SOLIDWORKS PART (.sldprt)
format: sldprt  version: not decoded by parser v0  size: 187,392 bytes
history: native  units: mm
features: sketch x6, plane x3, hole x2, material x1, extrude x1, cut_extrude x1 (+9 scaffold rows collapsed)
feature tree (23):
  scaffold x9  (default folders/planes/origin — collapsed)
  material  "Matériau <non spécifié>"
  plane  "Plan de face"
  plane  "Plan de dessus"
  plane  "Plan de droite"
  sketch  "Esquisse1"  dims[D1=40.0mm D2=4.0mm D3=14.0mm D4=6.0mm D5=12.0mm D6=6.0mm D7=4.0mm]
  extrude  "Boss.-Extru.1"  Depth=42.5mm
  hole  "Dégagement M31"  Diameter=3mm Depth=26mm
  sketch  "Esquisse4"  dims[D1=10.0mm D2=10.0mm]
  sketch  "Esquisse5"  dims[hole-wizard template sketch: 60 standard entries collapsed; hole parameters kept: c18.Profondeur du perçage jusqu'au prochain=26.0mm]
  hole  "Dégagement M33"  Diameter=3.2mm Depth=4mm
  sketch  "Esquisse7"  dims[c1.D1=~33.511672mm c1.D2=~32.666162mm c2.D1=4.0mm c2.D2=4.0mm c2.D3=4.0mm c2.D4=4.0mm]
  sketch  "Esquisse8"  dims[hole-wizard template sketch: 59 standard entries collapsed; hole parameters kept: c18.Diamètre du perçage jusqu'au prochain=3.2mm c18.Profondeur du perçage jusqu'au prochain=4.0mm]
  sketch  "Esquisse9"  dims[D1=3.5mm]
  cut_extrude  "Enlèv. mat.-Extru.1"  Depth=1mm
decode coverage: 10 of 10 modeling features carry decoded parameters
note: ~ marks probable driven/reference dimensions
note: suppression state not decoded; provenance and decode notes live in map.json
